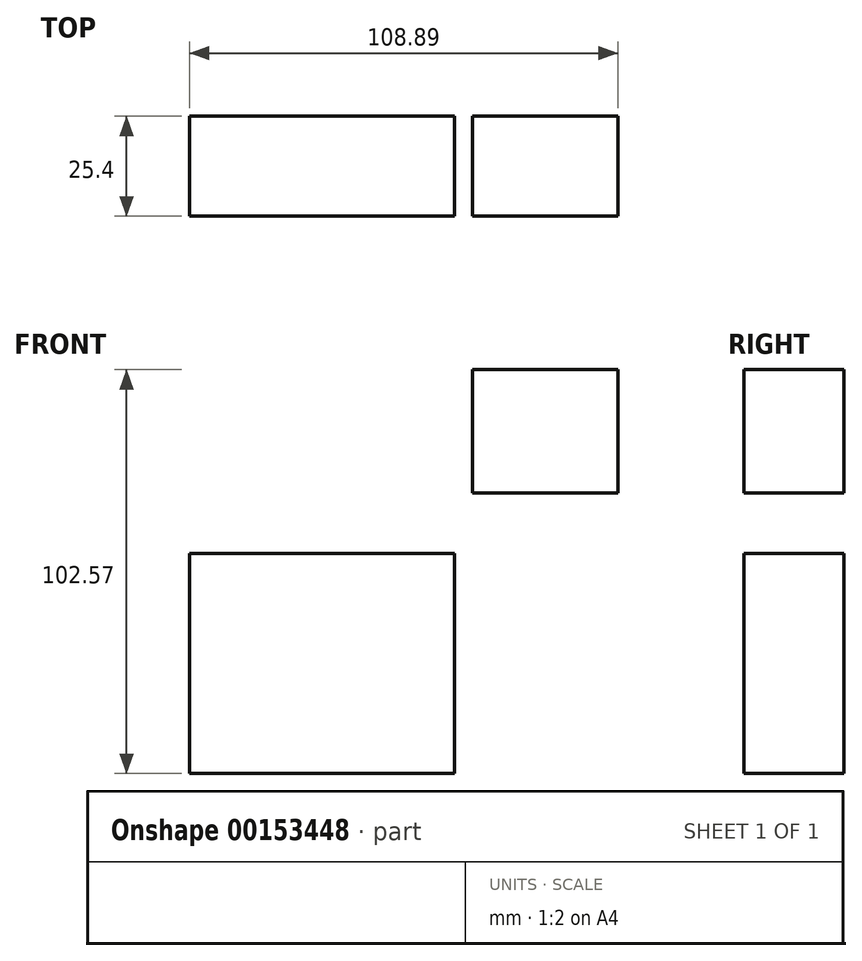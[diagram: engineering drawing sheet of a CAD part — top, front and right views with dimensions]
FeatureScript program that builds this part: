
annotation { "Feature Type Name" : "Feature", "Feature Type Description" : "" }
export const myFeature = defineFeature(function(context is Context, id is Id, definition is map)
    precondition{}
    {
        {
            var Q0;
            Q0=qCreatedBy(makeId("Front.planeOp"),FACE);
            var sketch = newSketch(context, id + "F0", { "sketchPlane" : qUnion([Q0])});
            skLineSegment(sketch, "E0.bottom", {"start": v(33.69, 27.96) * mm, "end": v(-33.69, 27.96) * mm});
            skLineSegment(sketch, "E0.top", {"start": v(33.69, -27.96) * mm, "end": v(-33.69, -27.96) * mm});
            skLineSegment(sketch, "E0.left", {"start": v(33.69, 27.96) * mm, "end": v(33.69, -27.96) * mm});
            skLineSegment(sketch, "E0.right", {"start": v(-33.69, 27.96) * mm, "end": v(-33.69, -27.96) * mm});
            skPoint(sketch, "E0.middle", {"position": v(0, 0) * mm});
            skSolve(sketch);
        }
        {
            var Q0;
            Q0=qCreatedBy(makeId("Front.planeOp"),FACE);
            var sketch = newSketch(context, id + "F1", { "sketchPlane" : qUnion([Q0])});
            skLineSegment(sketch, "E1.bottom", {"start": v(75.2, 43.22) * mm, "end": v(38.24, 43.22) * mm});
            skLineSegment(sketch, "E1.top", {"start": v(75.2, 74.6) * mm, "end": v(38.24, 74.6) * mm});
            skLineSegment(sketch, "E1.left", {"start": v(75.2, 43.22) * mm, "end": v(75.2, 74.6) * mm});
            skLineSegment(sketch, "E1.right", {"start": v(38.24, 43.22) * mm, "end": v(38.24, 74.6) * mm});
            skPoint(sketch, "E1.middle", {"position": v(56.72, 58.91) * mm});
            skSolve(sketch);
        }
        {
            var Q0;
            Q0=makeQuery(id+"F0.imprint","IMPRINT",FACE,{"disambiguationData":[TD([[makeQuery(id+"F0.imprint","IMPRINT",EDGE,{"derivedFrom":sQuery(id+"F0.wireOp",EDGE,"E0.bottom")}),1.0]])]});
            var Q1;
            Q1=makeQuery(id+"F1.imprint","IMPRINT",FACE,{"disambiguationData":[TD([[makeQuery(id+"F1.imprint","IMPRINT",EDGE,{"derivedFrom":sQuery(id+"F1.wireOp",EDGE,"E1.bottom")}),-1.0]])]});
            extrude(context, id + "F2", {"entities" : qUnion([Q0, Q1]), "depth" : 25.4 * mm});
        }
    });
